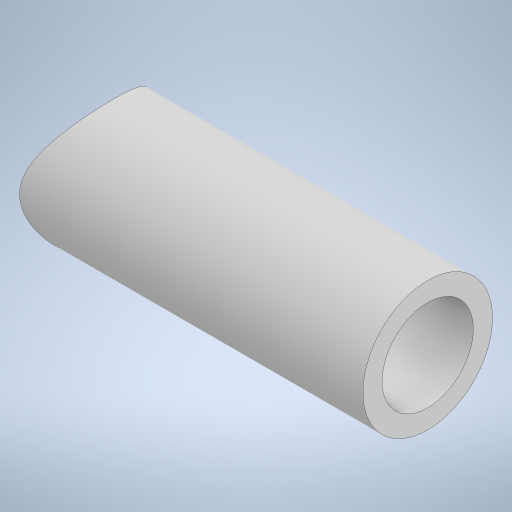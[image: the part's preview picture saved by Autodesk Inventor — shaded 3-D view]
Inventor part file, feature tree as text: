
AUTODESK INVENTOR PART (.ipt)
format: ipt  version: 2023 (Build 270158000, 158)  size: 229,376 bytes
history: native  units: in
note: dims shown in document units (in); Inventor stores cm internally (conversion verified against a paired STEP export)
features: extrude x2, sketch x2
ambient origin geometry x8: Origin, YZ Plane, XZ Plane, XY Plane, X Axis, Y Axis, Z Axis, Center Point
bodies: Solid1 (feature_tree)
feature tree (4):
  extrude  "Extrusion1"  Depth=0.066in
  extrude  "Extrusion2"  Depth=0.25in
  sketch  "Sketch1"  dims[d0=0.0938in d1=0.066in]
  sketch  "Sketch2"  dims[d2=0.25in d3=0.0in d4=0.125in d5=0.04in d6=0.25in d7=0.0in]
